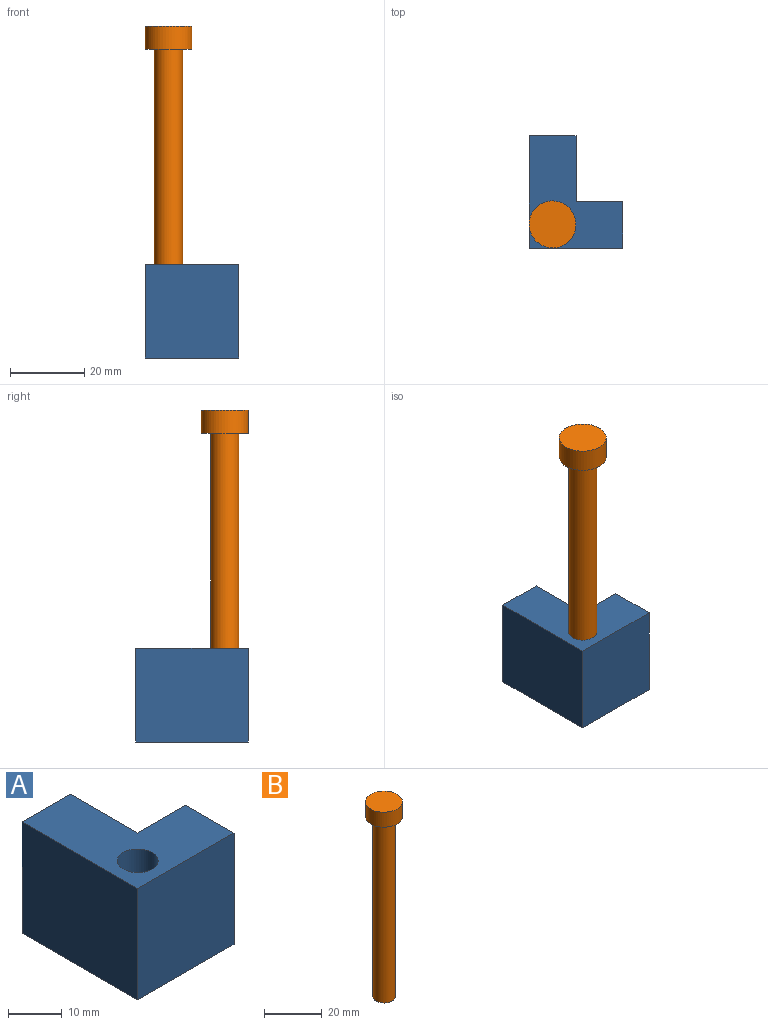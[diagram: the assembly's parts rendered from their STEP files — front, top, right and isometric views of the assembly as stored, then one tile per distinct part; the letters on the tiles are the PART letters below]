
ASSEMBLY  parts=2 mates=1
PART A: 9 faces, bbox 25.4x30.5x25.4 mm
  f0: plane 25.4x12.7mm, normal (0,1,0), area 322.6mm2, adj f1,f5,f6,f7
  f1: plane 30.48x25.4mm, normal (-1,0,0), area 774.2mm2, adj f0,f2,f6,f7
  f2: plane 25.4x25.4mm, normal (0,-1,0), area 645.2mm2, adj f1,f3,f6,f7
  f3: plane 25.4x12.7mm, normal (1,0,0), area 322.6mm2, adj f2,f4,f6,f7
  f4: plane 25.4x12.7mm, normal (0,1,0), area 322.6mm2, adj f3,f5,f6,f7
  f5: plane 25.4x17.78mm, normal (1,0,0), area 451.6mm2, adj f0,f4,f6,f7
  f6: plane 30.48x25.4mm, normal (0,0,1), area 502.8mm2, adj f0,f1,f2,f3,f4,f5,f8
  f7: plane 30.48x25.4mm, normal (0,0,-1), area 502.8mm2, adj f0,f1,f2,f3,f4,f5,f8
  f8: cylinder r=3.81mm len=25.4mm, axis (0,0,1), area 608mm2, adj f6,f7
PART B: 5 faces, bbox 12.7x12.7x82.6 mm
  f0: cylinder r=3.81mm len=76.2mm, axis (0,0,-1), area 1824.1mm2, adj f1,f4
  f1: plane 7.62x7.62mm, normal (0,0,-1), area 45.6mm2, adj f0
  f2: cylinder r=6.35mm len=12.7mm, axis (0,0,-1), area 253.4mm2, adj f3,f4
  f3: plane 12.7x12.7mm, normal (0,0,1), area 126.7mm2, adj f2
  f4: plane 12.7x12.7mm, normal (0,0,-1), area 81.1mm2, adj f0,f2
PLACE A t=(0.05,0.32,0.09)mm fixed
PLACE B rot(axis=(0,0,1),137deg) t=(4.3,56.77,7.26)mm
MATE cylindrical B.f0 <-> A.f8  axis (0,0,-1) through (6.4,6.67,7.26)mm
